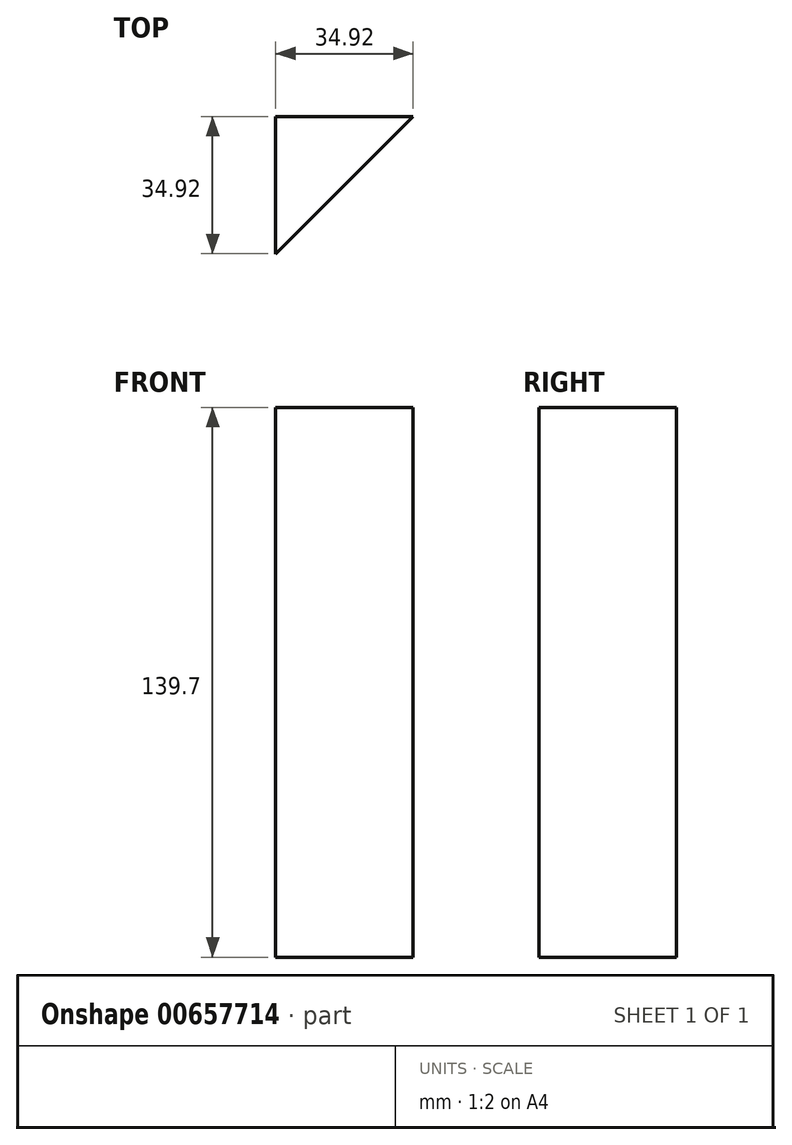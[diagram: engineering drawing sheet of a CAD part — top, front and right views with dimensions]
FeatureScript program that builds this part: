
annotation { "Feature Type Name" : "Feature", "Feature Type Description" : "" }
export const myFeature = defineFeature(function(context is Context, id is Id, definition is map)
    precondition{}
    {
        {
            var Q0;
            Q0=qCreatedBy(makeId("Top.planeOp"),FACE);
            var sketch = newSketch(context, id + "F0", { "sketchPlane" : qUnion([Q0])});
            skLineSegment(sketch, "E0", {"start": v(0, 0) * mm, "end": v(0, -34.93) * mm});
            skLineSegment(sketch, "E1", {"start": v(0, 0) * mm, "end": v(34.93, 0) * mm});
            skLineSegment(sketch, "E2", {"start": v(0, -34.92) * mm, "end": v(34.92, 0) * mm});
            skSolve(sketch);
        }
        {
            var Q0;
            Q0=makeQuery(id+"F0.imprint","IMPRINT",FACE,{"disambiguationData":[TD([[makeQuery(id+"F0.imprint","IMPRINT",EDGE,{"derivedFrom":sQuery(id+"F0.wireOp",EDGE,"E0")}),1.0]])]});
            extrude(context, id + "F1", {"entities" : qUnion([Q0]), "depth" : 139.7 * mm, "offsetDistance" : 25.4 * mm});
        }
    });
